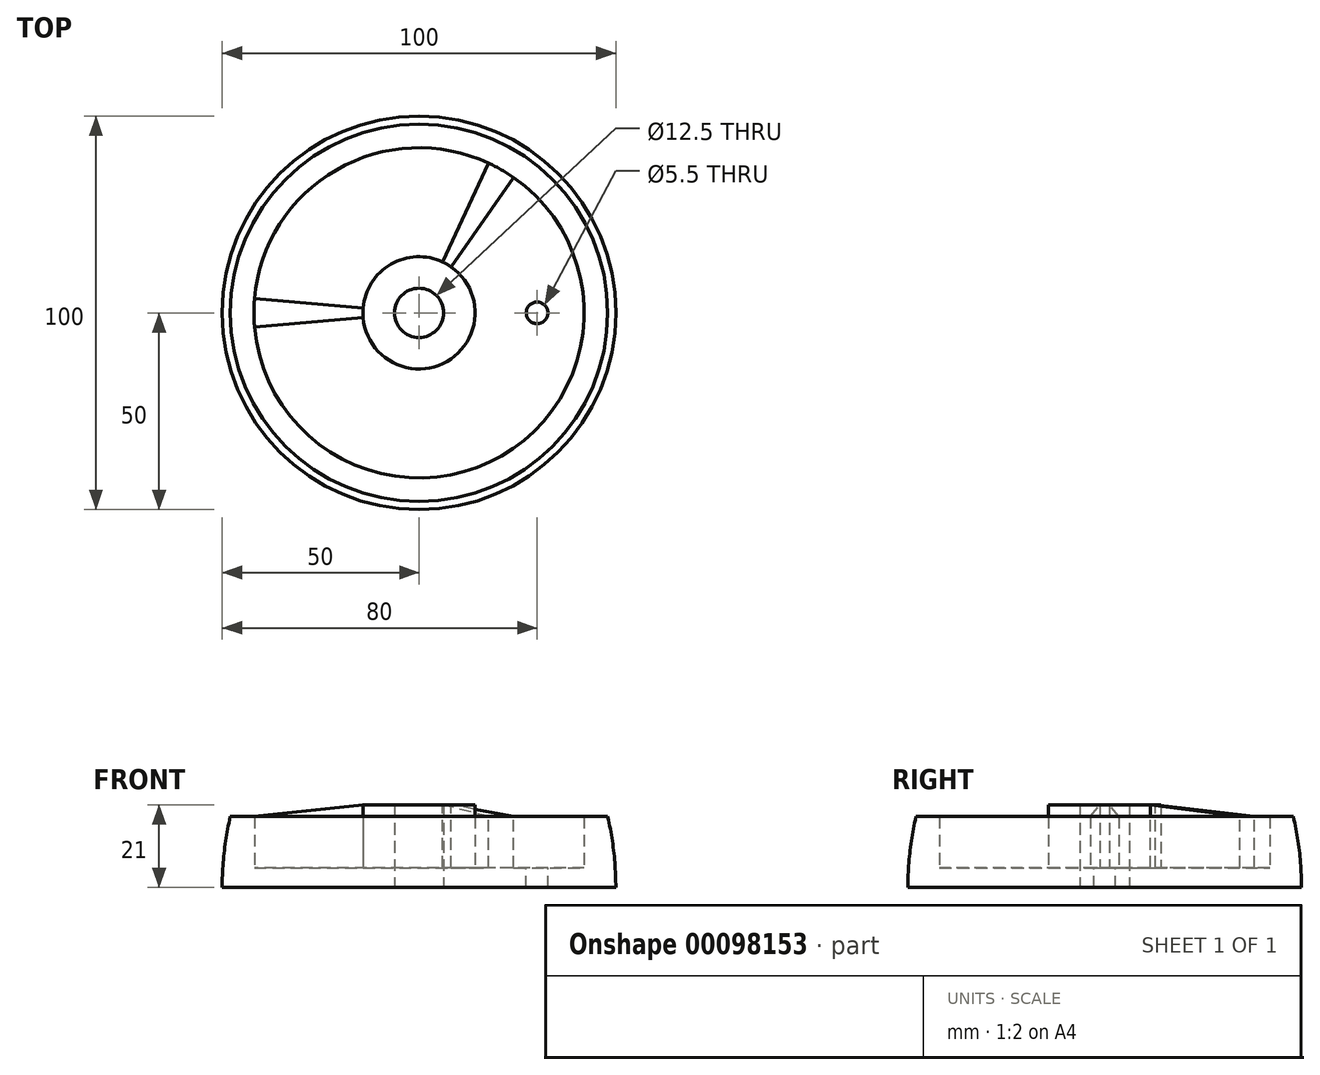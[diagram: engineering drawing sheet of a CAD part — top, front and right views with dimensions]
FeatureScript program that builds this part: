
annotation { "Feature Type Name" : "Feature", "Feature Type Description" : "" }
export const myFeature = defineFeature(function(context is Context, id is Id, definition is map)
    precondition{}
    {
        {
            var Q0;
            Q0=qCreatedBy(makeId("Front.planeOp"),FACE);
            var sketch = newSketch(context, id + "F0", { "sketchPlane" : qUnion([Q0])});
            skLineSegment(sketch, "E0", {"start": v(0, 0) * mm, "end": v(0, 17.05) * mm, "construction": true});
            skLineSegment(sketch, "E1", {"start": v(14.25, 5) * mm, "end": v(41.95, 5) * mm});
            skLineSegment(sketch, "E2", {"start": v(41.95, 5) * mm, "end": v(41.95, 18) * mm});
            skLineSegment(sketch, "E3", {"start": v(41.95, 18) * mm, "end": v(47.95, 18) * mm});
            skLineSegment(sketch, "E4", {"start": v(14.25, 5) * mm, "end": v(14.25, 21) * mm});
            skLineSegment(sketch, "E5", {"start": v(14.25, 21) * mm, "end": v(6.25, 21) * mm});
            skLineSegment(sketch, "E6", {"start": v(6.25, 21) * mm, "end": v(6.25, 0) * mm});
            skLineSegment(sketch, "E7", {"start": v(6.25, 0) * mm, "end": v(50, 0) * mm});
            skArc(sketch, "E8", {"start": v(50, 0) * mm, "mid": v(49.49, 9.06) * mm, "end": v(47.95, 18) * mm});
            skSolve(sketch);
        }
        {
            var Q0;
            Q0 = qSketchRegion(id + "F0", true);
            var Q1;
            Q1=sQuery(id+"F0.wireOp",EDGE,"E0");
            revolve(context, id + "F1", {"entities" : qUnion([Q0]), "axis" : qUnion([Q1]), "revolveType" : RevolveType.FULL});
        }
        {
            var Q0;
            Q0=qCreatedBy(makeId("Front.planeOp"),FACE);
            var sketch = newSketch(context, id + "F2", { "sketchPlane" : qUnion([Q0])});
            skLineSegment(sketch, "E9", {"start": v(-41.95, 18) * mm, "end": v(-41.95, 5) * mm});
            skLineSegment(sketch, "E10", {"start": v(-14.25, 21) * mm, "end": v(-14.25, 5) * mm});
            skLineSegment(sketch, "E11", {"start": v(-41.95, 18) * mm, "end": v(-14.25, 21) * mm});
            skLineSegment(sketch, "E12", {"start": v(-41.95, 5) * mm, "end": v(-14.25, 5) * mm});
            skSolve(sketch);
        }
        {
            var Q0;
            Q0 = qSketchRegion(id + "F2", true);
            var Q1;
            Q1=makeQuery(id+"F1.opRevolve","SWEPT_FACE",FACE,{"disambiguationData":[OSD([sQuery(id+"F0.wireOp",EDGE,"E4")])]});
            revolve(context, id + "F3", {"operationType" : NewBodyOperationType.ADD, "entities" : qUnion([Q0]), "axis" : qUnion([Q1]), "revolveType" : RevolveType.SYMMETRIC, "angle" : 10 * degree});
        }
        {
            var Q0;
            Q0=makeQuery(id+"F1.opRevolve","SWEPT_FACE",FACE,{"disambiguationData":[OSD([sQuery(id+"F0.wireOp",EDGE,"E1")])]});
            var sketch = newSketch(context, id + "F4", { "sketchPlane" : qUnion([Q0])});
            skPoint(sketch, "E13", {"position": v(30, 0) * mm});
            skSolve(sketch);
        }
        {
            var Q0;
            Q0=sQuery(id+"F4.wireOp",VERTEX,"E13");
            var Q1;
            Q1=makeQuery(id+"F1.opRevolve","SWEPT_BODY",BODY,{"disambiguationData":[OSD([sQuery(id+"F0.wireOp",EDGE,"E1"),sQuery(id+"F0.wireOp",EDGE,"E2"),sQuery(id+"F0.wireOp",EDGE,"E3"),sQuery(id+"F0.wireOp",EDGE,"E4"),sQuery(id+"F0.wireOp",EDGE,"E5"),sQuery(id+"F0.wireOp",EDGE,"E6"),sQuery(id+"F0.wireOp",EDGE,"E7"),sQuery(id+"F0.wireOp",EDGE,"E8")])]});
            hole(context, id + "F5", {"style" : HoleStyle.SIMPLE, "endStyle" : HoleEndStyle.THROUGH, "standardTappedOrClearance" : lookupTablePath({ "standard" : "ISO", "fit" : "Normal", "size" : "M5", "type" : "Clearance" }), "standardBlindInLast" : lookupTablePath({ "fit" : "Standard", "standard" : "ISO", "size" : "M5", "type" : "Clearance" }), "holeDiameter" : 5.5 * mm, "locations" : qUnion([Q0]), "scope" : qUnion([Q1]), "isTappedThrough" : true});
        }
        {
            var Q0;
            Q0=qCreatedBy(makeId("Front.planeOp"),FACE);
            var Q1;
            {var subQ0=sQuery(id+"F2.wireOp",EDGE,"E11");var subQ1=sQuery(id+"F2.wireOp",EDGE,"E12");var subQ2=sQuery(id+"F2.wireOp",EDGE,"E10");var subQ3=sQuery(id+"F2.wireOp",EDGE,"E9");Q1=makeQuery(id+"FrZ8SWs77KroVgF_1.1.F3.boolean.opBoolean","SPLIT",FACE,{"disambiguationData":[TD([makeQuery(id+"F3.opRevolve","CAP_FACE",FACE,{"disambiguationData":[OSD([subQ3,subQ2,subQ0,subQ1])],"isStart":false})])],"derivedFrom":makeQuery(id+"F1.opRevolve","SWEPT_FACE",FACE,{"disambiguationData":[OSD([sQuery(id+"F0.wireOp",EDGE,"E4")])]})});}
            cPlane(context, id + "F6", {"entities" : qUnion([Q0, Q1]), "cplaneType" : CPlaneType.LINE_ANGLE, "offset" : 150 * mm, "angle" : 120 * degree, "width" : 150 * mm, "height" : 150 * mm});
        }
        {
            var Q0;
            Q0=qCreatedBy(id+"F6.planeOp",FACE);
            var sketch = newSketch(context, id + "F7", { "sketchPlane" : qUnion([Q0])});
            skLineSegment(sketch, "E14", {"start": v(41.95, 5) * mm, "end": v(41.95, 18) * mm});
            skLineSegment(sketch, "E15", {"start": v(14.25, 5) * mm, "end": v(14.25, 21) * mm});
            skLineSegment(sketch, "E16", {"start": v(41.95, 18) * mm, "end": v(14.25, 21) * mm});
            skLineSegment(sketch, "E17", {"start": v(41.95, 5) * mm, "end": v(14.25, 5) * mm});
            skSolve(sketch);
        }
        {
            var Q0;
            Q0=makeQuery(id+"F7.imprint","IMPRINT",FACE,{"disambiguationData":[TD([[makeQuery(id+"F7.imprint","IMPRINT",EDGE,{"derivedFrom":sQuery(id+"F7.wireOp",EDGE,"E14")}),1.0]])]});
            var Q1;
            Q1=sQuery(id+"F7.wireOp",EDGE,"E16");
            var Q2;
            {var subQ0=sQuery(id+"F2.wireOp",EDGE,"E11");var subQ1=sQuery(id+"F2.wireOp",EDGE,"E12");var subQ2=sQuery(id+"F2.wireOp",EDGE,"E10");var subQ3=sQuery(id+"F2.wireOp",EDGE,"E9");Q2=makeQuery(id+"FrZ8SWs77KroVgF_1.1.F3.boolean.opBoolean","SPLIT",FACE,{"disambiguationData":[TD([makeQuery(id+"F3.opRevolve","CAP_FACE",FACE,{"disambiguationData":[OSD([subQ3,subQ2,subQ0,subQ1])],"isStart":false})])],"derivedFrom":makeQuery(id+"F1.opRevolve","SWEPT_FACE",FACE,{"disambiguationData":[OSD([sQuery(id+"F0.wireOp",EDGE,"E4")])]})});}
            revolve(context, id + "F8", {"operationType" : NewBodyOperationType.ADD, "entities" : qUnion([Q0]), "surfaceEntities" : qUnion([Q1]), "axis" : qUnion([Q2]), "revolveType" : RevolveType.SYMMETRIC, "angle" : 10 * degree});
        }
    });
